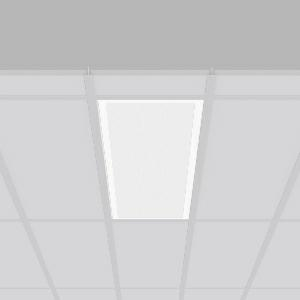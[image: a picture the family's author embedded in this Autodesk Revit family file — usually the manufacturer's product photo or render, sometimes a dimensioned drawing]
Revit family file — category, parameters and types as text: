
# Revit family: sidelite_eco_312368_002_790_06fe
name_source: partatom
category: Lighting Fixtures
units: mm (PartAtom-declared; Revit-internal decimal feet)

## family parameters
Cut with Voids When Loaded = No
Host = Face
Light Source = No
Part Type = Normal
Room Calculation Point = No
Round Connector Dimension = Use Diameter
Shared = No

## types (1)
- MultiLumen 1 (1 x LED Modul 830, 3200 lm, 3000)
    Apparent Load = 29 VA
    CIE Flux Codes = 64 88 97 100 100
    Color Rendering = 80
    Color Temperature = 3000
    Default Elevation = 1800 mm
    Description = Series: SIDELITE ECO
Highly economical recessed luminaire with progressive LED technology. Frame made of aluminium, powder-coated. Diffuser plastic microprismatic. Lightguide and diffuser made of non-yellowing plastic (PMMA). Lateral light emission (RZB SIDELITE technology) for homogeneous light distribution. External driver. External driver with simple plug-in locking system and extended converter connecting cable to luminaire (1.90 m). MultiLumen: 4 steps adjustable luminous flux. Factory setting is the lowest offered step. Luminaire can be used with accessories (to be ordered separately) as recessed or surface mounting luminaire. Perfect for office areas (RUG < 19) and environments with computer screens in accordance with EN 12464-1. Qualified for use in the food and drink industry. 
Colour: white
Length: 1245 mm
Width: 308 mm
Cut-out length: 1233 mm
Cut-out width: 296 mm
Recess height: 160 mm
Luminaire: recess height: 37 mm
Lamp: LED
Socket: without socket
Colour temperature: 3000K
Colour rendering index (CRI): 80
System power: 29 W
Rated luminous flux: 3200 lm
Luminous efficiency: 110 lm/W
System power 2: 33 W
Rated luminous flux 2: 3500 lm
Luminous efficiency 2: 106 lm/W
System power 3: 35 W
Rated luminous flux 3: 3700 lm
Luminous efficiency 3: 106 lm/W
System power 4: 38 W
Rated luminous flux 4: 4000 lm
Luminous efficiency 4: 105 lm/W
Control gear: Regulated power supply
Protection class: II
Type of protection: IP 40
    Height = 0 mm  [stored 0 ft]
    Lamp = 1 x LED Modul 830
    Lamp Light Flux = 3200 lm
    Lamp count = 1
    Length = 1245 mm
    Lifetime = 50000 h
    Luminous efficacy = 110 lm/W
    Manufacturer = RZB
    ModVariant = No
    Model = 312368.002.790
    Mounting Place = Ceiling
    Mounting Type = Recessed
    Number of Poles = 1
    OnlyDefault = Yes
    Power Factor = 1
    Product Name = SIDELITE ECO
    Product group = Recessed modular luminaires
    ProductGroupID = 406
    Protection Class = Protection class II
    Protection Degree = IP 20
    RLX_Detail_Level = 1
    RLX_Emergency_Light_Flux = 0 lm
    RLX_Emergency_Type = 0
    RLX_Emergency_Type_DB = No
    RlxData = <blob elided: 36029 chars, md5=7204776d>
    Socket = socket
    Standby Power = 0 W
    System Light Flux = 3200 lm
    System Power = 29 W
    Type Comments = MultiLumen 1
    Type Image = 312368.002.jpg
    URL = http://relux.com
    VarID = multilumen_1
    Voltage = 230 V
    Voltage Range = 220-240 V
    Weight = 0.00 kg
    Width = 308 mm

note: [stored X ft] marks values corroborated as IEEE doubles in the binary element streams (Revit-internal decimal feet)

## geometry (parser evidence)
native form markers: Blend x4, Sweep x11
no freeform markers — native parametric forms only
